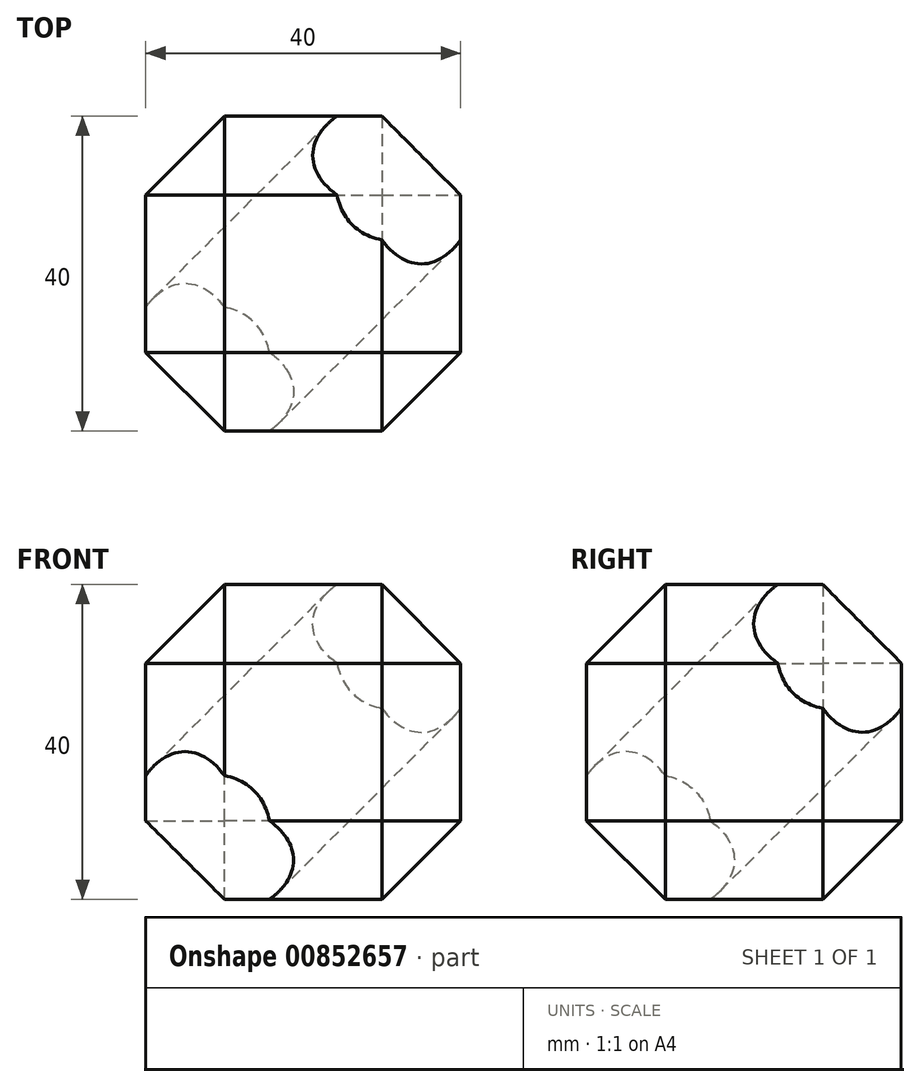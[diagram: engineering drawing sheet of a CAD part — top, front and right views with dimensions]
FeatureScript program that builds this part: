
annotation { "Feature Type Name" : "Feature", "Feature Type Description" : "" }
export const myFeature = defineFeature(function(context is Context, id is Id, definition is map)
    precondition{}
    {
        {
            var Q0;
            Q0=qCreatedBy(makeId("Top.planeOp"),FACE);
            var sketch = newSketch(context, id + "F0", { "sketchPlane" : qUnion([Q0])});
            skLineSegment(sketch, "E0.bottom", {"start": v(20, -20) * mm, "end": v(-20, -20) * mm});
            skLineSegment(sketch, "E0.top", {"start": v(20, 20) * mm, "end": v(-20, 20) * mm});
            skLineSegment(sketch, "E0.left", {"start": v(20, -20) * mm, "end": v(20, 20) * mm});
            skLineSegment(sketch, "E0.right", {"start": v(-20, -20) * mm, "end": v(-20, 20) * mm});
            skPoint(sketch, "E0.middle", {"position": v(0, 0) * mm});
            skSolve(sketch);
        }
        {
            var Q0;
            Q0=makeQuery(id+"F0.imprint","IMPRINT",FACE,{"disambiguationData":[TD([[makeQuery(id+"F0.imprint","IMPRINT",EDGE,{"derivedFrom":sQuery(id+"F0.wireOp",EDGE,"E0.bottom")}),-1.0]])]});
            extrude(context, id + "F1", {"entities" : qUnion([Q0]), "depth" : 40 * mm, "offsetDistance" : 25 * mm});
        }
        {
            var Q0;
            Q0=makeQuery(id+"F1.opExtrude","CAP_FACE",FACE,{"disambiguationData":[OSD([sQuery(id+"F0.wireOp",EDGE,"E0.bottom"),sQuery(id+"F0.wireOp",EDGE,"E0.top"),sQuery(id+"F0.wireOp",EDGE,"E0.left"),sQuery(id+"F0.wireOp",EDGE,"E0.right")])],"isStart":false});
            var Q1;
            Q1=makeQuery(id+"F1.opExtrude","CAP_FACE",FACE,{"disambiguationData":[OSD([sQuery(id+"F0.wireOp",EDGE,"E0.bottom"),sQuery(id+"F0.wireOp",EDGE,"E0.top"),sQuery(id+"F0.wireOp",EDGE,"E0.left"),sQuery(id+"F0.wireOp",EDGE,"E0.right")])],"isStart":true});
            var Q2;
            Q2=makeQuery(id+"F1.opExtrude","SWEPT_EDGE",EDGE,{"disambiguationData":[OSD([sQuery(id+"F0.wireOp",EDGE,"E0.bottom"),sQuery(id+"F0.wireOp",EDGE,"E0.left")])]});
            var Q3;
            Q3=makeQuery(id+"F1.opExtrude","SWEPT_EDGE",EDGE,{"disambiguationData":[OSD([sQuery(id+"F0.wireOp",EDGE,"E0.bottom"),sQuery(id+"F0.wireOp",EDGE,"E0.right")])]});
            var Q4;
            Q4=makeQuery(id+"F1.opExtrude","SWEPT_EDGE",EDGE,{"disambiguationData":[OSD([sQuery(id+"F0.wireOp",EDGE,"E0.top"),sQuery(id+"F0.wireOp",EDGE,"E0.left")])]});
            var Q5;
            Q5=makeQuery(id+"F1.opExtrude","SWEPT_EDGE",EDGE,{"disambiguationData":[OSD([sQuery(id+"F0.wireOp",EDGE,"E0.top"),sQuery(id+"F0.wireOp",EDGE,"E0.right")])]});
            chamfer(context, id + "F2", {"entities" : qUnion([Q0, Q1, Q2, Q3, Q4, Q5]), "width" : 10 * mm, "tangentPropagation" : true});
        }
        {
            var Q0;
            {var subQ0=sQuery(id+"F0.wireOp",EDGE,"E0.left");var subQ1=sQuery(id+"F0.wireOp",EDGE,"E0.top");Q0=makeQuery(id+"F2.opChamfer","BLEND_FACE",FACE,{"disambiguationData":[OSD([subQ1,subQ0]),TDD([makeQuery(id+"F1.opExtrude","CAP_VERTEX",VERTEX,{"disambiguationData":[OSD([subQ1,subQ0])],"isStart":false})])]});}
            var sketch = newSketch(context, id + "F3", { "sketchPlane" : qUnion([Q0])});
            skLineSegment(sketch, "E1", {"start": v(12.25, 14.14) * mm, "end": v(0, 14.14) * mm});
            skLineSegment(sketch, "E2", {"start": v(6.12, 17.68) * mm, "end": v(12.25, 7.07) * mm});
            skPoint(sketch, "E3", {"position": v(8.16, 14.14) * mm});
            skSolve(sketch);
        }
        {
            var Q0;
            Q0=sQuery(id+"F3.wireOp",VERTEX,"E3");
            var Q1;
            Q1=makeQuery(id+"F1.opExtrude","SWEPT_BODY",BODY,{"disambiguationData":[OSD([sQuery(id+"F0.wireOp",EDGE,"E0.bottom"),sQuery(id+"F0.wireOp",EDGE,"E0.top"),sQuery(id+"F0.wireOp",EDGE,"E0.left"),sQuery(id+"F0.wireOp",EDGE,"E0.right")])]});
            hole(context, id + "F4", {"style" : HoleStyle.SIMPLE, "endStyle" : HoleEndStyle.THROUGH, "holeDiameter" : 22.5 * mm, "majorDiameter" : 5 * mm, "isTappedThrough" : true, "tappedDepth" : 12 * mm, "tapClearance" : 3, "locations" : qUnion([Q0]), "scope" : qUnion([Q1])});
        }
    });
